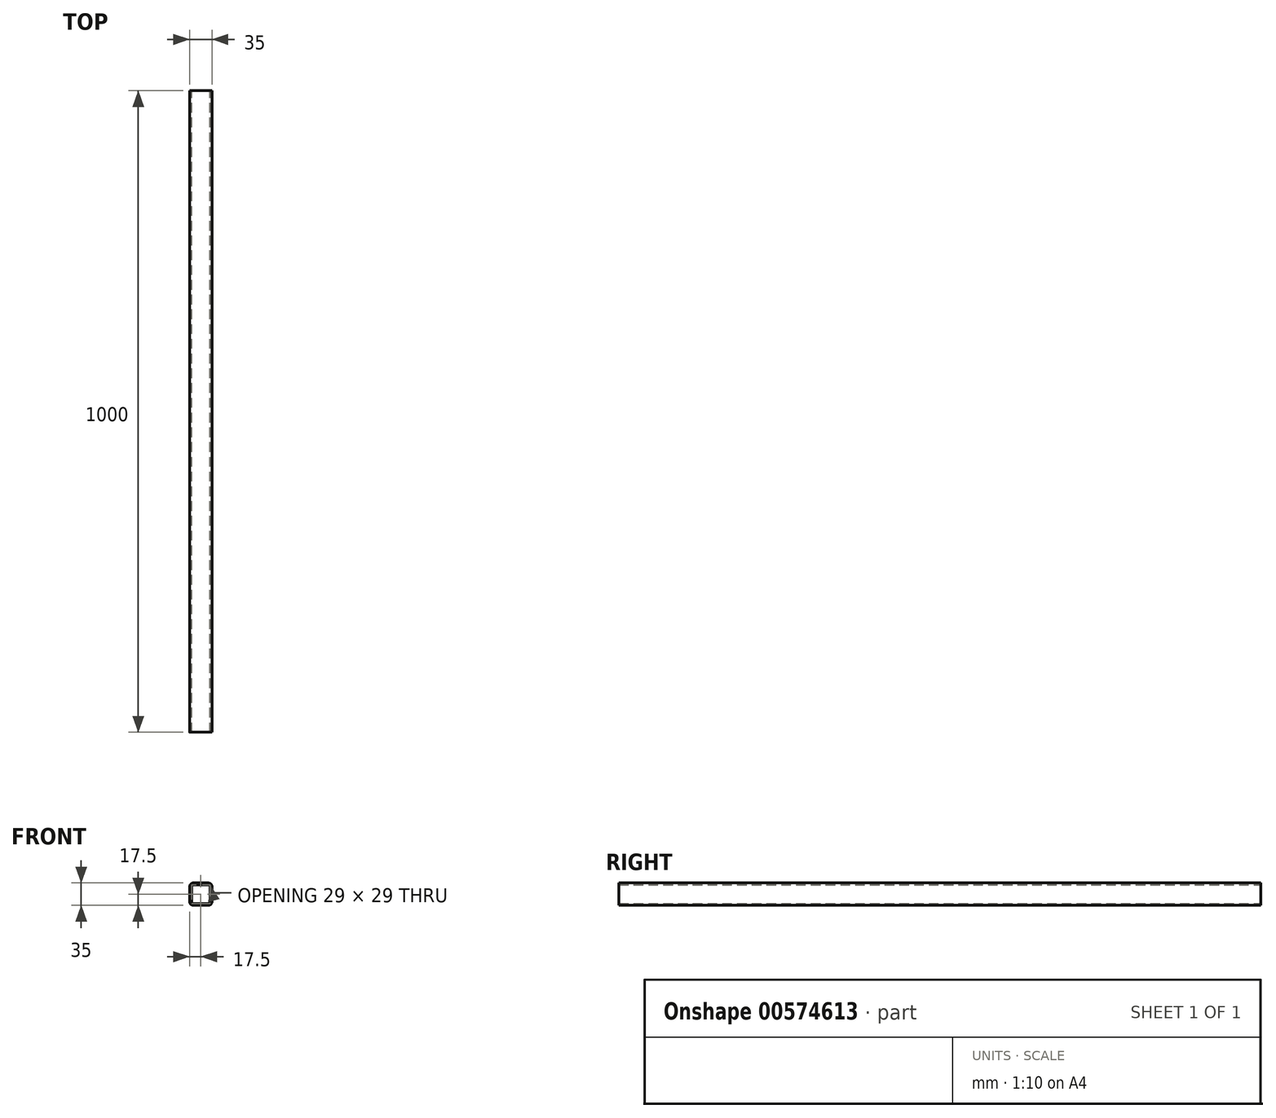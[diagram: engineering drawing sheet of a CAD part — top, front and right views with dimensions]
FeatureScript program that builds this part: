
annotation { "Feature Type Name" : "Feature", "Feature Type Description" : "" }
export const myFeature = defineFeature(function(context is Context, id is Id, definition is map)
    precondition{}
    {
        {
            var Q0;
            Q0=qCreatedBy(makeId("Front.planeOp"),FACE);
            var sketch = newSketch(context, id + "F0", { "sketchPlane" : qUnion([Q0])});
            skLineSegment(sketch, "E0.bottom", {"start": v(6, 0) * mm, "end": v(29, 0) * mm});
            skLineSegment(sketch, "E0.top", {"start": v(6, 35) * mm, "end": v(29, 35) * mm});
            skLineSegment(sketch, "E0.left", {"start": v(0, 6) * mm, "end": v(0, 29) * mm});
            skLineSegment(sketch, "E0.right", {"start": v(35, 6) * mm, "end": v(35, 29) * mm});
            skPoint(sketch, "E1.visualSharp", {"position": v(0, 35) * mm});
            skArc(sketch, "E1.filletArc", {"start": v(6, 35) * mm, "mid": v(1.76, 33.24) * mm, "end": v(0, 29) * mm});
            skPoint(sketch, "E2.visualSharp", {"position": v(35, 35) * mm});
            skArc(sketch, "E2.filletArc", {"start": v(35, 29) * mm, "mid": v(33.24, 33.24) * mm, "end": v(29, 35) * mm});
            skPoint(sketch, "E3.visualSharp", {"position": v(35, 0) * mm});
            skArc(sketch, "E3.filletArc", {"start": v(29, 0) * mm, "mid": v(33.24, 1.76) * mm, "end": v(35, 6) * mm});
            skPoint(sketch, "E4.visualSharp", {"position": v(0, 0) * mm});
            skArc(sketch, "E4.filletArc", {"start": v(0, 6) * mm, "mid": v(1.76, 1.76) * mm, "end": v(6, 0) * mm});
            skArc(sketch, "E5.0", {"start": v(6, 32) * mm, "mid": v(3.88, 31.12) * mm, "end": v(3, 29) * mm});
            skLineSegment(sketch, "E5.1", {"start": v(3, 6) * mm, "end": v(3, 29) * mm});
            skLineSegment(sketch, "E5.2", {"start": v(6, 32) * mm, "end": v(29, 32) * mm});
            skArc(sketch, "E5.3", {"start": v(3, 6) * mm, "mid": v(3.88, 3.88) * mm, "end": v(6, 3) * mm});
            skArc(sketch, "E5.4", {"start": v(32, 29) * mm, "mid": v(31.12, 31.12) * mm, "end": v(29, 32) * mm});
            skLineSegment(sketch, "E5.5", {"start": v(32, 6) * mm, "end": v(32, 29) * mm});
            skArc(sketch, "E5.6", {"start": v(29, 3) * mm, "mid": v(31.12, 3.88) * mm, "end": v(32, 6) * mm});
            skLineSegment(sketch, "E5.7", {"start": v(6, 3) * mm, "end": v(29, 3) * mm});
            skSolve(sketch);
        }
        {
            var Q0;
            Q0=makeQuery(id+"F0.imprint","IMPRINT",FACE,{"disambiguationData":[TD([[makeQuery(id+"F0.imprint","IMPRINT",EDGE,{"derivedFrom":sQuery(id+"F0.wireOp",EDGE,"E0.bottom")}),1.0]])]});
            extrude(context, id + "F1", {"entities" : qUnion([Q0]), "depth" : 1000 * mm, "offsetDistance" : 25 * mm});
        }
    });
